# Revit family: NU-640 Class II Type A2 Animal Handling BSC
name_source: partatom
category: Mechanical Equipment
units: mm (PartAtom-declared; Revit-internal decimal feet)

## family parameters
Always vertical = Yes
Cut with Voids When Loaded = No
OmniClass Number = 23.75.00.00
OmniClass Title = Climate Control (HVAC)
Part Type = Normal
Room Calculation Point = No
Round Connector Dimension = Use Diameter
Shared = No
Work Plane-Based = No

## types (3) — shared parameters
Cabinet Height = 3' - 10 9/16"
Default Elevation = 0' - 0"
Depth = 2' - 5 1/2"
Description = LabGard ES Energy Saver Class II, Type A2 Animal Handling Biosafety Cainet
Manufacturer = Nuaire Inc.

## per-type parameters (varying)
| type | Base Width | Exhaust Filter | Interior Width | Model | Width | caster width |
| NU-640-600 | 6' - 5 13/32" | 3' - 4 1/2" | 5' - 10 1/2" | NU-640-600 Class II Type A2 BSC | 6' - 2 11/16" | 6' - 1 1/8" |
| NU-640-500 | 5' - 5 13/32" | 2' - 10 1/2" | 4' - 10 1/2" | NU-640-500 Class II Type A2 BSC | 5' - 2 11/16" | 5' - 1 1/8" |
| NU-640-400 | 4' - 5 13/32" | 2' - 4 1/2" | 3' - 10 1/2" | NU-640-400 Class II Type A2 BSC | 4' - 2 11/16" | 4' - 1 1/8" |

## geometry (parser evidence)
native form markers: Sweep x1
no freeform markers — native parametric forms only
